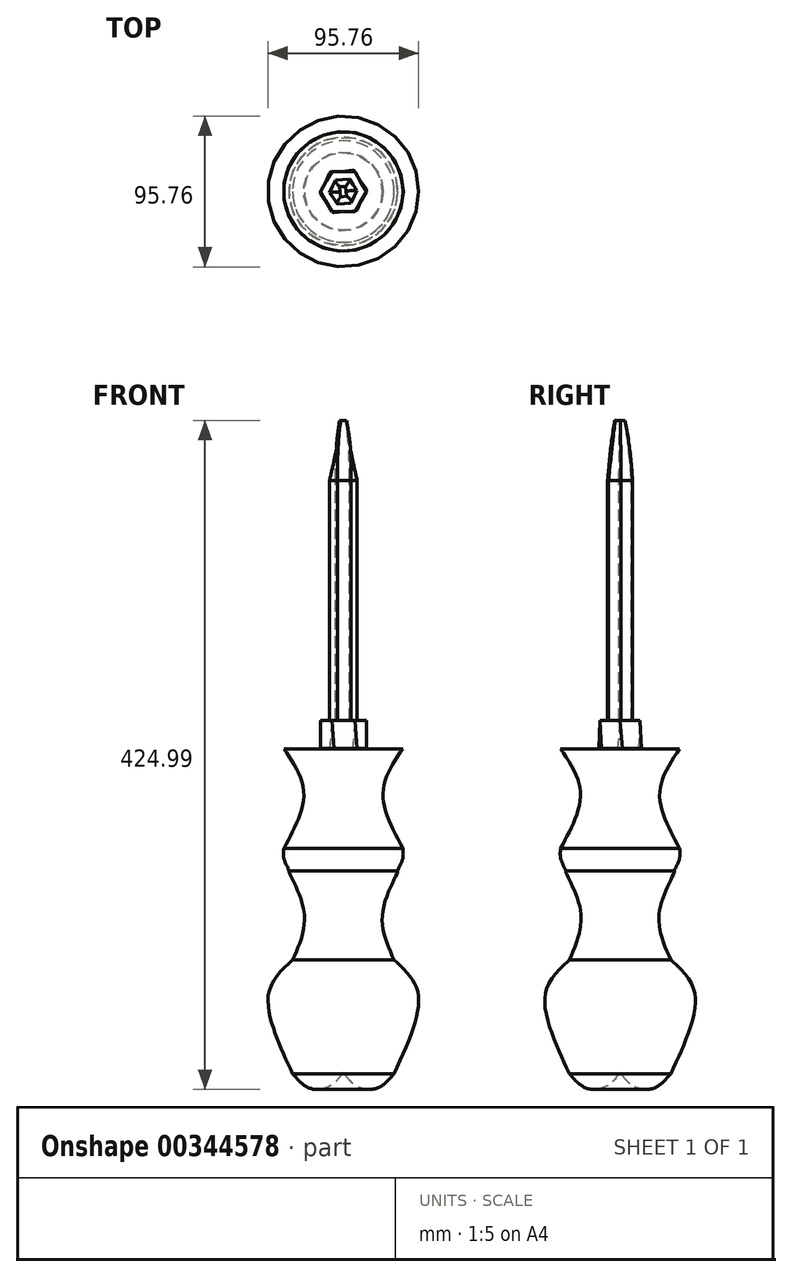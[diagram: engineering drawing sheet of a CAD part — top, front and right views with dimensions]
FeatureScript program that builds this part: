
annotation { "Feature Type Name" : "Feature", "Feature Type Description" : "" }
export const myFeature = defineFeature(function(context is Context, id is Id, definition is map)
    precondition{}
    {
        {
            var Q0;
            Q0=qCreatedBy(makeId("Front.planeOp"),FACE);
            var sketch = newSketch(context, id + "F0", { "sketchPlane" : qUnion([Q0])});
            skFitSpline(sketch, "E0", {"points": [v(0, 102.56) * mm, v(0, -103.03) * mm, v(0, -104.04) * mm], "startDerivative": vector(0, -315.6) * mm, "endDerivative": vector(0, -8.73) * mm});
            skFitSpline(sketch, "E1", {"points": [v(0, -103.03) * mm, v(-8.43, -111.64) * mm, v(-21.09, -113.16) * mm, v(-32.23, -103.85) * mm], "startDerivative": vector(-22.73, -30.8) * mm, "endDerivative": vector(-29.03, 33.5) * mm});
            skFitSpline(sketch, "E2", {"points": [v(-32.23, -31.63) * mm, v(-25.14, 0) * mm, v(-34.4, 24.07) * mm, v(-34.4, 25.08) * mm], "startDerivative": vector(27.9, 62.88) * mm, "endDerivative": vector(2.75, 8.03) * mm});
            skLineSegment(sketch, "E3", {"start": v(0, 102.56) * mm, "end": v(-37.8, 102.56) * mm});
            skPoint(sketch, "E4.4.internal.orphan", {"position": v(-37.8, 39.26) * mm});
            skFitSpline(sketch, "E5", {"points": [v(-37.8, 39.26) * mm, v(-37.8, 33.18) * mm, v(-34.4, 25.08) * mm], "startDerivative": vector(-1.41, -13.05) * mm, "endDerivative": vector(7.91, -15.24) * mm});
            skLineSegment(sketch, "E6", {"start": v(0, 135.47) * mm, "end": v(0, -146.07) * mm, "construction": true});
            skFitSpline(sketch, "E7", {"points": [v(-32.23, -103.85) * mm, v(-47.56, -53.34) * mm, v(-32.23, -31.63) * mm], "startDerivative": vector(-44.7, 96.32) * mm, "endDerivative": vector(50.07, 45.22) * mm});
            skFitSpline(sketch, "E8", {"points": [v(-37.8, 39.26) * mm, v(-25.14, 74.33) * mm, v(-37.8, 102.56) * mm], "startDerivative": vector(37.47, 69.05) * mm, "endDerivative": vector(-38.65, 57.36) * mm});
            skSolve(sketch);
        }
        {
            var Q0;
            Q0 = qSketchRegion(id + "F0", true);
            var Q1;
            Q1=sQuery(id+"F0.wireOp",EDGE,"E6");
            revolve(context, id + "F1", {"entities" : qUnion([Q0]), "axis" : qUnion([Q1]), "revolveType" : RevolveType.FULL});
        }
        {
            var Q0;
            Q0=qCreatedBy(makeId("Top.planeOp"),FACE);
            cPlane(context, id + "F2", {"entities" : qUnion([Q0]), "cplaneType" : CPlaneType.OFFSET, "offset" : 102.87 * mm, "width" : 152.4 * mm, "height" : 152.4 * mm});
        }
        {
            var Q0;
            Q0=qCreatedBy(id+"F2.planeOp",FACE);
            var sketch = newSketch(context, id + "F3", { "sketchPlane" : qUnion([Q0])});
            skCircle(sketch, "E9.cCircle", {"center": v(0, 0) * mm, "radius": 12.7 * mm, "construction": true});
            skLineSegment(sketch, "E9.0", {"start": v(5.86, 13.44) * mm, "end": v(14.57, 1.64) * mm});
            skLineSegment(sketch, "E9.1", {"start": v(14.57, 1.64) * mm, "end": v(8.7, -11.8) * mm});
            skLineSegment(sketch, "E9.2", {"start": v(8.7, -11.8) * mm, "end": v(-5.86, -13.44) * mm});
            skLineSegment(sketch, "E9.3", {"start": v(-5.86, -13.44) * mm, "end": v(-14.57, -1.64) * mm});
            skLineSegment(sketch, "E9.4", {"start": v(-14.57, -1.64) * mm, "end": v(-8.7, 11.8) * mm});
            skLineSegment(sketch, "E9.5", {"start": v(-8.7, 11.8) * mm, "end": v(5.86, 13.44) * mm});
            skPoint(sketch, "E9.0.midPoint", {"position": v(10.22, 7.54) * mm});
            skSolve(sketch);
        }
        {
            var Q0;
            Q0=qCreatedBy(id+"F2.planeOp",FACE);
            cPlane(context, id + "F4", {"entities" : qUnion([Q0]), "cplaneType" : CPlaneType.OFFSET, "offset" : 17.78 * mm, "width" : 152.4 * mm, "height" : 152.4 * mm});
        }
        {
            var Q0;
            Q0=qCreatedBy(id+"F4.planeOp",FACE);
            var sketch = newSketch(context, id + "F5", { "sketchPlane" : qUnion([Q0])});
            skCircle(sketch, "E10.cCircle", {"center": v(0, 0) * mm, "radius": 12.7 * mm, "construction": true});
            skLineSegment(sketch, "E10.0", {"start": v(7.33, -12.7) * mm, "end": v(-7.33, -12.7) * mm});
            skLineSegment(sketch, "E10.1", {"start": v(-7.33, -12.7) * mm, "end": v(-14.66, 0) * mm});
            skLineSegment(sketch, "E10.2", {"start": v(-14.66, 0) * mm, "end": v(-7.33, 12.7) * mm});
            skLineSegment(sketch, "E10.3", {"start": v(-7.33, 12.7) * mm, "end": v(7.33, 12.7) * mm});
            skLineSegment(sketch, "E10.4", {"start": v(7.33, 12.7) * mm, "end": v(14.66, 0) * mm});
            skLineSegment(sketch, "E10.5", {"start": v(14.66, 0) * mm, "end": v(7.33, -12.7) * mm});
            skPoint(sketch, "E10.0.midPoint", {"position": v(0, -12.7) * mm});
            skSolve(sketch);
        }
        {
            var Q0;
            Q0=makeQuery(id+"F5.imprint","IMPRINT",FACE,{"disambiguationData":[TD([[makeQuery(id+"F5.imprint","IMPRINT",EDGE,{"derivedFrom":sQuery(id+"F5.wireOp",EDGE,"E10.0")}),-1.0]])]});
            var Q1;
            Q1=makeQuery(id+"F3.imprint","IMPRINT",FACE,{"disambiguationData":[TD([[makeQuery(id+"F3.imprint","IMPRINT",EDGE,{"derivedFrom":sQuery(id+"F3.wireOp",EDGE,"E9.0")}),-1.0]])]});
            loft(context, id + "F6", {"sheetProfilesArray" : [{ "sheetProfileEntities" : qUnion([Q0]) }, { "sheetProfileEntities" : qUnion([Q1]) }]});
        }
        {
            var Q0;
            Q0=qCreatedBy(id+"F4.planeOp",FACE);
            var sketch = newSketch(context, id + "F7", { "sketchPlane" : qUnion([Q0])});
            skCircle(sketch, "E11.cCircle", {"center": v(0, 0) * mm, "radius": 7.62 * mm, "construction": true});
            skLineSegment(sketch, "E11.0", {"start": v(-3.84, -7.92) * mm, "end": v(-8.78, -0.64) * mm});
            skLineSegment(sketch, "E11.1", {"start": v(-8.78, -0.64) * mm, "end": v(-4.94, 7.28) * mm});
            skLineSegment(sketch, "E11.2", {"start": v(-4.94, 7.28) * mm, "end": v(3.84, 7.92) * mm});
            skLineSegment(sketch, "E11.3", {"start": v(3.84, 7.92) * mm, "end": v(8.78, 0.64) * mm});
            skLineSegment(sketch, "E11.4", {"start": v(8.78, 0.64) * mm, "end": v(4.94, -7.28) * mm});
            skLineSegment(sketch, "E11.5", {"start": v(4.94, -7.28) * mm, "end": v(-3.84, -7.92) * mm});
            skPoint(sketch, "E11.0.midPoint", {"position": v(-6.3, -4.28) * mm});
            skSolve(sketch);
        }
        {
            var Q0;
            Q0=qCreatedBy(id+"F4.planeOp",FACE);
            cPlane(context, id + "F8", {"entities" : qUnion([Q0]), "cplaneType" : CPlaneType.OFFSET, "offset" : 152.4 * mm, "width" : 152.4 * mm, "height" : 152.4 * mm});
        }
        {
            var Q0;
            Q0=qCreatedBy(id+"F8.planeOp",FACE);
            var sketch = newSketch(context, id + "F9", { "sketchPlane" : qUnion([Q0])});
            skCircle(sketch, "E12.cCircle", {"center": v(0, 0) * mm, "radius": 7.62 * mm, "construction": true});
            skLineSegment(sketch, "E12.0", {"start": v(8.77, 0.69) * mm, "end": v(4.98, -7.25) * mm});
            skLineSegment(sketch, "E12.1", {"start": v(4.98, -7.25) * mm, "end": v(-3.8, -7.94) * mm});
            skLineSegment(sketch, "E12.2", {"start": v(-3.8, -7.94) * mm, "end": v(-8.77, -0.69) * mm});
            skLineSegment(sketch, "E12.3", {"start": v(-8.77, -0.69) * mm, "end": v(-4.98, 7.25) * mm});
            skLineSegment(sketch, "E12.4", {"start": v(-4.98, 7.25) * mm, "end": v(3.8, 7.94) * mm});
            skLineSegment(sketch, "E12.5", {"start": v(3.8, 7.94) * mm, "end": v(8.77, 0.69) * mm});
            skPoint(sketch, "E12.0.midPoint", {"position": v(6.88, -3.28) * mm});
            skSolve(sketch);
        }
        {
            var Q1;
            Q1=makeQuery(id+"F7.imprint","IMPRINT",FACE,{"disambiguationData":[TD([[makeQuery(id+"F7.imprint","IMPRINT",EDGE,{"derivedFrom":sQuery(id+"F7.wireOp",EDGE,"E11.0")}),-1.0]])]});
            var Q2;
            Q2=makeQuery(id+"F9.imprint","IMPRINT",FACE,{"disambiguationData":[TD([[makeQuery(id+"F9.imprint","IMPRINT",EDGE,{"derivedFrom":sQuery(id+"F9.wireOp",EDGE,"E12.0")}),-1.0]])]});
            loft(context, id + "F10", {"operationType" : NewBodyOperationType.ADD, "sheetProfilesArray" : [{ "sheetProfileEntities" : qUnion([Q1]) }, { "sheetProfileEntities" : qUnion([Q2]) }]});
        }
        {
            var Q0;
            Q0=qCreatedBy(id+"F8.planeOp",FACE);
            cPlane(context, id + "F11", {"entities" : qUnion([Q0]), "cplaneType" : CPlaneType.OFFSET, "offset" : 25.4 * mm, "width" : 152.4 * mm, "height" : 152.4 * mm});
        }
        {
            var Q0;
            Q0=qCreatedBy(id+"F11.planeOp",FACE);
            cPlane(context, id + "F12", {"entities" : qUnion([Q0]), "cplaneType" : CPlaneType.OFFSET, "offset" : 12.7 * mm, "width" : 152.4 * mm, "height" : 152.4 * mm});
        }
        {
            var Q0;
            Q0=qCreatedBy(id+"F12.planeOp",FACE);
            var sketch = newSketch(context, id + "F13", { "sketchPlane" : qUnion([Q0])});
            skLineSegment(sketch, "E13", {"start": v(-2.42, 2.97) * mm, "end": v(-2.1, -0.23) * mm});
            skLineSegment(sketch, "E14", {"start": v(-1.76, -3.43) * mm, "end": v(2.02, -3.04) * mm});
            skLineSegment(sketch, "E15", {"start": v(2.02, -3.04) * mm, "end": v(1.7, 0.08) * mm});
            skLineSegment(sketch, "E16", {"start": v(-2.42, 2.97) * mm, "end": v(1.38, 3.2) * mm});
            skLineSegment(sketch, "E17", {"start": v(-2.1, -0.23) * mm, "end": v(-1.76, -3.43) * mm});
            skLineSegment(sketch, "E18", {"start": v(1.7, 0.08) * mm, "end": v(1.38, 3.2) * mm});
            skSolve(sketch);
        }
        {
            var Q0;
            Q0=qCreatedBy(id+"F11.planeOp",FACE);
            var sketch = newSketch(context, id + "F14", { "sketchPlane" : qUnion([Q0])});
            skLineSegment(sketch, "E19", {"start": v(-4.05, 4.78) * mm, "end": v(-3.56, -0.26) * mm});
            skLineSegment(sketch, "E20", {"start": v(-3.07, -5.3) * mm, "end": v(4, -4.62) * mm});
            skLineSegment(sketch, "E21", {"start": v(4, -4.62) * mm, "end": v(3.52, 0.35) * mm});
            skLineSegment(sketch, "E22", {"start": v(-4.05, 4.78) * mm, "end": v(3.03, 5.32) * mm});
            skLineSegment(sketch, "E23", {"start": v(-3.56, -0.26) * mm, "end": v(-3.07, -5.3) * mm});
            skLineSegment(sketch, "E24", {"start": v(3.52, 0.35) * mm, "end": v(3.03, 5.32) * mm});
            skSolve(sketch);
        }
        {
            var Q1;
            Q1=makeQuery(id+"F10.opLoft","CAP_FACE",FACE,{"disambiguationData":[OSD([makeQuery(id+"F9.imprint","IMPRINT",FACE,{"disambiguationData":[TD([[makeQuery(id+"F9.imprint","IMPRINT",EDGE,{"derivedFrom":sQuery(id+"F9.wireOp",EDGE,"E12.0")}),-1.0]])]})])],"isStart":true});
            var Q2;
            Q2=makeQuery(id+"F14.imprint","IMPRINT",FACE,{"disambiguationData":[TD([[makeQuery(id+"F14.imprint","IMPRINT",EDGE,{"derivedFrom":sQuery(id+"F14.wireOp",EDGE,"E19")}),1.0]])]});
            var Q3;
            Q3=makeQuery(id+"F13.imprint","IMPRINT",FACE,{"disambiguationData":[TD([[makeQuery(id+"F13.imprint","IMPRINT",EDGE,{"derivedFrom":sQuery(id+"F13.wireOp",EDGE,"E13")}),1.0]])]});
            loft(context, id + "F15", {"operationType" : NewBodyOperationType.ADD, "sheetProfilesArray" : [{ "sheetProfileEntities" : qUnion([Q1]) }, { "sheetProfileEntities" : qUnion([Q2]) }, { "sheetProfileEntities" : qUnion([Q3]) }]});
        }
    });
